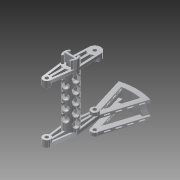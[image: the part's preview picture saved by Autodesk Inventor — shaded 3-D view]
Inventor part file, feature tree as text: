
AUTODESK INVENTOR PART (.ipt)
format: ipt  version: 2014 (Build 180170000, 170)  size: 1,210,880 bytes
history: native  units: mm
features: extrude x13, sketch x8, fillet x3, plane x1, chamfer x1, mirror x1, pattern_linear x1
ambient origin geometry x8: Origin, YZ Plane, XZ Plane, XY Plane, X Axis, Y Axis, Z Axis, Center Point
bodies: Solid1 (feature_tree)
feature tree (28):
  sketch  "Sketch1"  dims[d2=4.0mm d3=6.35mm]
  extrude  "Extrusion1"  Depth=6.35mm
  extrude  "Extrusion2"  Depth=13.0mm
  extrude  "Extrusion3"  Depth=4.0mm
  plane  "Work Plane1"
  extrude  "Extrusion4"  Depth=2.0mm
  extrude  "Extrusion5"  Depth=2.0mm
  extrude  "Extrusion6"  Depth=45.0mm
  extrude  "Extrusion7"  Depth=4.0mm
  extrude  "Extrusion8"  Depth=2.0mm
  extrude  "Extrusion9"  Depth=2.0mm
  extrude  "Extrusion10"  Depth=10.0mm
  fillet  "Fillet1"  Radius=6.0mm
  fillet  "Fillet2"  Radius=12.0mm
  extrude  "Extrusion11"  TaperAngle=0.0deg  [1 undecoded]
  fillet  "Fillet3"  Radius=108.0mm
  extrude  "Extrusion12"  Depth=10.0mm
  chamfer  "Chamfer1"  Distance=5.0mm
  sketch  "Sketch7"  dims[d14=6.5mm d15=45.0mm]
  sketch  "Sketch8"  dims[d16=6.35mm d17=4.0mm]
  extrude  "Extrusion13"  Depth=10.0mm
  mirror  "Mirror1"
  pattern_linear  "Rectangular Pattern2"  Spacing1=5.0mm  [1 undecoded]
  sketch  "Sketch3"  dims[d5=13.0mm d7=4.0mm]
  sketch  "Sketch4"  dims[d8=4.0mm d9=4.0mm]
  sketch  "Sketch5"  dims[d10=4.0mm d11=2.0mm]
  sketch  "Sketch6"  dims[d12=2.0mm d13=4.0mm]
  sketch  "Sketch9"  dims[d18=4.0mm d19=2.0mm d20=2.0mm d21=45.0mm d22=6.0mm d23=0.0mm d24=12.0mm d25=0.0mm d27=0.0mm d28=108.0mm d31=10.0mm d34=5.0mm d35=5.0mm d36=5.0mm d37=5.0mm d38=10.0mm d39=45.0deg d40=4.0mm d41=4.0mm d42=4.0mm d43=2.0mm d44=4.0mm d45=6.0mm d46=0.0mm d47=12.0mm d48=0.0mm d49=10.0mm d50=10.0mm d51=30.0mm d52=30.0mm d53=10.0mm d54=62.0mm d55=6.0mm d56=0.0mm d57=27.0mm d58=0.0mm d59=21.0mm d60=0.0mm d62=6.0mm d63=0.0mm d64=14.0mm d65=30.0mm d66=0.0mm d70=14.0mm d71=14.0mm d72=14.0mm d73=14.0mm d74=4.333333mm d75=4.333333mm d76=4.333333mm d77=4.333333mm d78=4.333333mm d79=4.333333mm d80=13.0mm d81=13.0mm d82=13.0mm d83=13.0mm d84=13.0mm d85=13.0mm d86=14.0mm d87=4.333333mm d88=14.0mm d89=14.0mm d90=14.0mm d91=4.333333mm d92=4.333333mm d93=26.5mm d94=26.5mm d95=30.0mm d96=0.0mm d97=1.0mm d98=1.0mm d99=4.0mm d100=2.0mm d101=2.0mm d102=45.0deg d103=45.0deg d104=15.0mm d105=0.0mm d106=1.0mm d107=32.0mm d108=26.0mm d109=7.5mm d110=8.774964mm d111=8.774964mm d112=4.0mm d113=10.0mm d114=0.0mm d115=90.0mm d116=6.0mm d117=2.0mm d118=45.0deg d119=150.0mm d120=2.0mm d121=12.763383mm d122=12.763383mm d123=7.433393mm d124=7.433393mm d125=7.433393mm d126=10.0mm d127=10.0mm d128=10.0mm d129=10.0mm d130=7.433393mm d131=7.433393mm d132=2.0mm d133=2.0mm d134=10.0mm d135=0.0mm d136=20.0mm d138=27.0mm]
note: 2 required parameter values undecoded (feature->parameter linkage not recoverable at this tier; creation-order binding heuristic only, values carry confidence <= 0.55)
